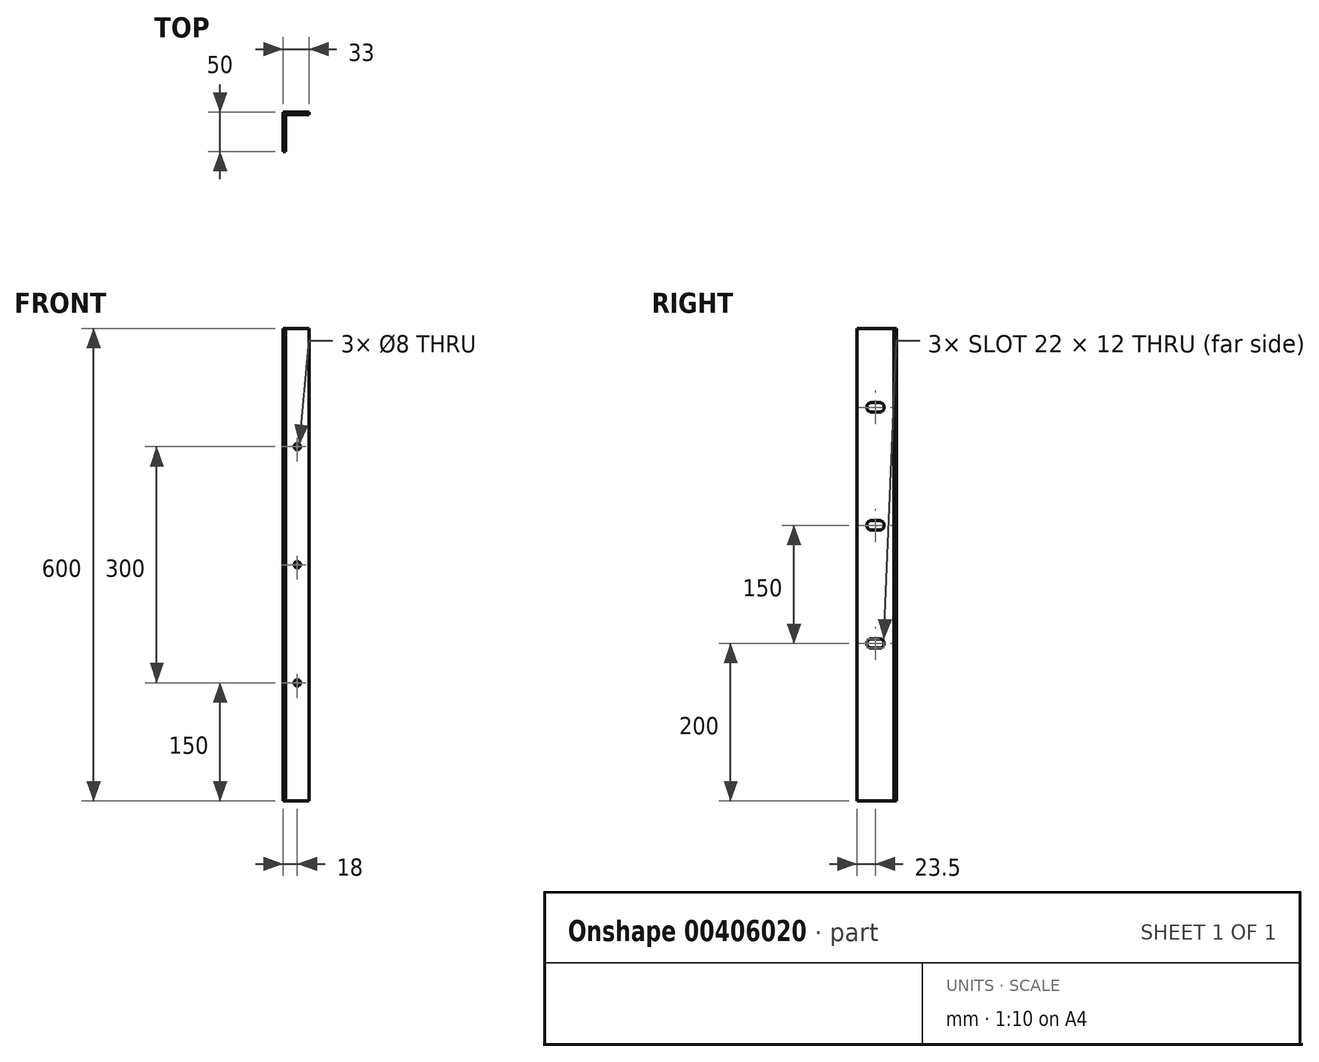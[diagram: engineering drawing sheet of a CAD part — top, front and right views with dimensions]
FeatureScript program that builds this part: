
annotation { "Feature Type Name" : "Feature", "Feature Type Description" : "" }
export const myFeature = defineFeature(function(context is Context, id is Id, definition is map)
    precondition{}
    {
        {
            var Q0;
            Q0=qCreatedBy(makeId("Top.planeOp"),FACE);
            var sketch = newSketch(context, id + "F0", { "sketchPlane" : qUnion([Q0])});
            skLineSegment(sketch, "E0", {"start": v(0, 0) * mm, "end": v(0, -50) * mm});
            skLineSegment(sketch, "E1", {"start": v(0, -50) * mm, "end": v(3, -50) * mm});
            skLineSegment(sketch, "E2", {"start": v(3, -50) * mm, "end": v(3, -3) * mm});
            skLineSegment(sketch, "E3", {"start": v(3, -3) * mm, "end": v(33, -3) * mm});
            skLineSegment(sketch, "E4", {"start": v(33, -3) * mm, "end": v(33, 0) * mm});
            skLineSegment(sketch, "E5", {"start": v(33, 0) * mm, "end": v(0, 0) * mm});
            skSolve(sketch);
        }
        {
            var Q0;
            Q0 = qSketchRegion(id + "F0", true);
            extrude(context, id + "F1", {"entities" : qUnion([Q0]), "depth" : 600 * mm});
        }
        {
            var Q0;
            Q0=makeQuery(id+"F1.opExtrude","SWEPT_FACE",FACE,{"disambiguationData":[OSD([sQuery(id+"F0.wireOp",EDGE,"E3")])]});
            var sketch = newSketch(context, id + "F2", { "sketchPlane" : qUnion([Q0])});
            skLineSegment(sketch, "E6", {"start": v(33, 600) * mm, "end": v(18, 600) * mm, "construction": true});
            skLineSegment(sketch, "E7", {"start": v(18, 600) * mm, "end": v(18, 0) * mm, "construction": true});
            skCircle(sketch, "E8", {"center": v(18, 150) * mm, "radius": 4 * mm});
            skCircle(sketch, "E9", {"center": v(18, 300) * mm, "radius": 4 * mm});
            skCircle(sketch, "E10", {"center": v(18, 450) * mm, "radius": 4 * mm});
            skSolve(sketch);
        }
        {
            var Q0;
            Q0 = qSketchRegion(id + "F2", true);
            extrude(context, id + "F3", {"entities" : qUnion([Q0]), "operationType" : NewBodyOperationType.REMOVE, "endBound" : BoundingType.THROUGH_ALL, "oppositeDirection" : true, "depth" : 25 * mm});
        }
        {
            var Q0;
            Q0=makeQuery(id+"F1.opExtrude","SWEPT_FACE",FACE,{"disambiguationData":[OSD([sQuery(id+"F0.wireOp",EDGE,"E2")])]});
            var sketch = newSketch(context, id + "F4", { "sketchPlane" : qUnion([Q0])});
            skLineSegment(sketch, "E11", {"start": v(-50, 600) * mm, "end": v(-26.5, 600) * mm, "construction": true});
            skLineSegment(sketch, "E12", {"start": v(-26.5, 0) * mm, "end": v(-26.5, 600) * mm, "construction": true});
            skLineSegment(sketch, "E13", {"start": v(-31.5, 506) * mm, "end": v(-21.5, 506) * mm});
            skLineSegment(sketch, "E14", {"start": v(-31.5, 494) * mm, "end": v(-21.5, 494) * mm});
            skArc(sketch, "E15", {"start": v(-31.5, 506) * mm, "mid": v(-37.5, 500) * mm, "end": v(-31.5, 494) * mm});
            skArc(sketch, "E16", {"start": v(-21.5, 494) * mm, "mid": v(-15.5, 500) * mm, "end": v(-21.5, 506) * mm});
            skLineSegment(sketch, "E17", {"start": v(-31.5, 356) * mm, "end": v(-21.5, 356) * mm});
            skLineSegment(sketch, "E18", {"start": v(-31.5, 344) * mm, "end": v(-21.5, 344) * mm});
            skArc(sketch, "E19", {"start": v(-31.5, 356) * mm, "mid": v(-37.5, 350) * mm, "end": v(-31.5, 344) * mm});
            skArc(sketch, "E20", {"start": v(-21.5, 344) * mm, "mid": v(-15.5, 350) * mm, "end": v(-21.5, 356) * mm});
            skLineSegment(sketch, "E21", {"start": v(-31.5, 206) * mm, "end": v(-21.5, 206) * mm});
            skLineSegment(sketch, "E22", {"start": v(-31.5, 206) * mm, "end": v(-31.5, 206) * mm});
            skLineSegment(sketch, "E23", {"start": v(-21.5, 206) * mm, "end": v(-21.5, 206) * mm});
            skArc(sketch, "E24", {"start": v(-31.5, 206) * mm, "mid": v(-37.5, 200) * mm, "end": v(-31.5, 194) * mm});
            skLineSegment(sketch, "E25", {"start": v(-31.5, 194) * mm, "end": v(-21.5, 194) * mm});
            skArc(sketch, "E26", {"start": v(-21.5, 206) * mm, "mid": v(-15.5, 200) * mm, "end": v(-21.5, 194) * mm});
            skSolve(sketch);
        }
        {
            var Q0;
            Q0 = qSketchRegion(id + "F4", true);
            extrude(context, id + "F5", {"entities" : qUnion([Q0]), "operationType" : NewBodyOperationType.REMOVE, "endBound" : BoundingType.THROUGH_ALL, "oppositeDirection" : true, "depth" : 25 * mm});
        }
    });
